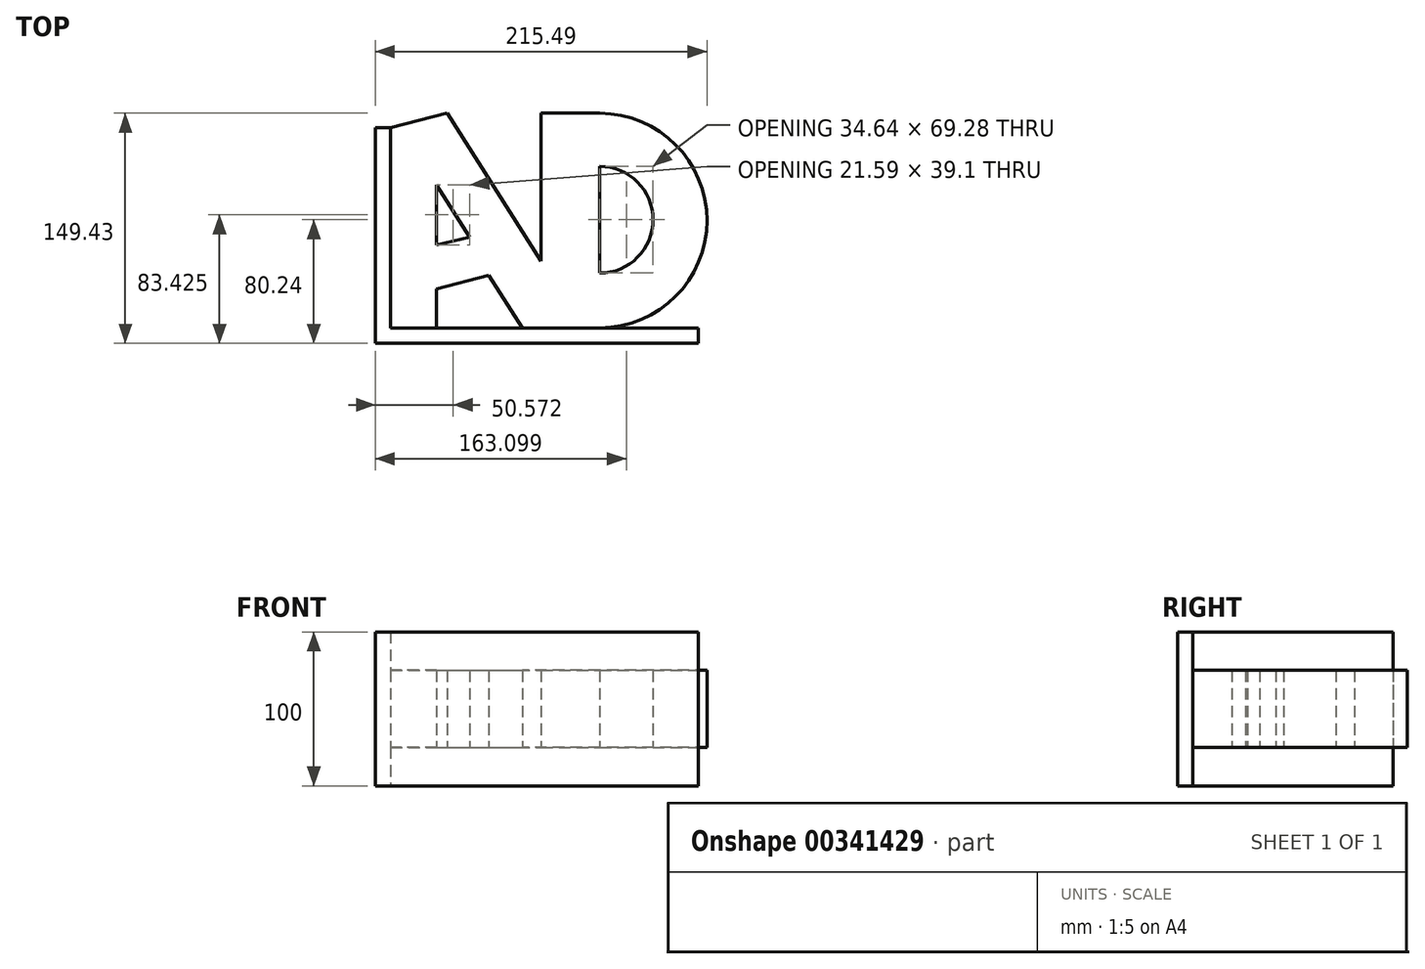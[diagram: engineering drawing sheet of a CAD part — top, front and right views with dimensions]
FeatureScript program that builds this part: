
annotation { "Feature Type Name" : "Feature", "Feature Type Description" : "" }
export const myFeature = defineFeature(function(context is Context, id is Id, definition is map)
    precondition{}
    {
        {
            var Q0;
            Q0=qCreatedBy(makeId("Top.planeOp"),FACE);
            var sketch = newSketch(context, id + "F0", { "sketchPlane" : qUnion([Q0])});
            skLineSegment(sketch, "E0", {"start": v(-97.78, 0) * mm, "end": v(102.22, 0) * mm});
            skLineSegment(sketch, "E1", {"start": v(-97.78, 10) * mm, "end": v(-97.78, 140) * mm});
            skLineSegment(sketch, "E2", {"start": v(-97.78, 140) * mm, "end": v(-60.97, 149.43) * mm});
            skLineSegment(sketch, "E3", {"start": v(-60.97, 149.43) * mm, "end": v(0, 53.26) * mm});
            skLineSegment(sketch, "E4", {"start": v(0, 53.26) * mm, "end": v(0, 149.43) * mm});
            skLineSegment(sketch, "E5", {"start": v(0, 149.43) * mm, "end": v(38, 149.43) * mm});
            skLineSegment(sketch, "E6", {"start": v(102.22, 0) * mm, "end": v(102.22, 10) * mm});
            skLineSegment(sketch, "E7", {"start": v(102.22, 10) * mm, "end": v(38, 10) * mm});
            skArc(sketch, "E8", {"start": v(38, 149.43) * mm, "mid": v(107.71, 79.71) * mm, "end": v(38, 10) * mm});
            skLineSegment(sketch, "E9", {"start": v(38, 114.88) * mm, "end": v(38, 45.6) * mm});
            skArc(sketch, "E10", {"start": v(38, 114.88) * mm, "mid": v(72.64, 80.24) * mm, "end": v(38, 45.6) * mm});
            skPoint(sketch, "E11.end.orphan", {"position": v(0, 114.88) * mm});
            skPoint(sketch, "E12.start.orphan", {"position": v(0, 10) * mm});
            skPoint(sketch, "E13.end.orphan", {"position": v(-8.4, 10) * mm});
            skPoint(sketch, "E14.start.orphan", {"position": v(-68, 10) * mm});
            skPoint(sketch, "E15.end.orphan", {"position": v(-26.25, 10) * mm});
            skPoint(sketch, "E16.end.orphan", {"position": v(-19.02, 10) * mm});
            skPoint(sketch, "E17.start.orphan", {"position": v(-56.9, 10) * mm});
            skPoint(sketch, "E18.orphan", {"position": v(-35.1, 10) * mm});
            skLineSegment(sketch, "E19", {"start": v(-68, 10) * mm, "end": v(-68, 35.4) * mm});
            skLineSegment(sketch, "E20", {"start": v(-68, 35.4) * mm, "end": v(-33.96, 44.12) * mm});
            skLineSegment(sketch, "E21", {"start": v(-33.96, 44.12) * mm, "end": v(-12.33, 10) * mm});
            skLineSegment(sketch, "E22", {"start": v(-12.33, 10) * mm, "end": v(-68, 10) * mm});
            skPoint(sketch, "E23.start.orphan", {"position": v(-68, 63.88) * mm});
            skLineSegment(sketch, "E24", {"start": v(-68, 63.88) * mm, "end": v(-68, 102.98) * mm});
            skLineSegment(sketch, "E25", {"start": v(-68, 102.98) * mm, "end": v(-46.41, 68.92) * mm});
            skLineSegment(sketch, "E26", {"start": v(-68, 63.88) * mm, "end": v(-46.41, 68.92) * mm});
            skLineSegment(sketch, "E27", {"start": v(38, 10) * mm, "end": v(-12.33, 10) * mm});
            skLineSegment(sketch, "E28", {"start": v(-68, 10) * mm, "end": v(-97.78, 10) * mm});
            skLineSegment(sketch, "E29", {"start": v(-97.78, 0) * mm, "end": v(-107.78, 0) * mm});
            skLineSegment(sketch, "E30", {"start": v(-107.78, 0) * mm, "end": v(-107.78, 140) * mm});
            skLineSegment(sketch, "E31", {"start": v(-107.78, 140) * mm, "end": v(-97.78, 140) * mm});
            skSolve(sketch);
        }
        {
            var Q0;
            Q0=makeQuery(id+"F0.imprint","IMPRINT",FACE,{"disambiguationData":[TD([[makeQuery(id+"F0.imprint","IMPRINT",EDGE,{"derivedFrom":sQuery(id+"F0.wireOp",EDGE,"E0")}),1.0]])]});
            extrude(context, id + "F1", {"entities" : qUnion([Q0]), "depth" : 100 * mm});
        }
        {
            var Q0;
            {var subQ0=sQuery(id+"F0.wireOp",EDGE,"E2");Q0=makeQuery(id+"F0.imprint","IMPRINT",FACE,{"disambiguationData":[TD([[makeQuery(id+"F0.imprint","IMPRINT",EDGE,{"derivedFrom":subQ0}),-1.0]])]});}
            extrude(context, id + "F2", {"entities" : qUnion([Q0]), "operationType" : NewBodyOperationType.ADD, "depth" : 75 * mm});
        }
        {
            var Q0;
            {var subQ0=sQuery(id+"F0.wireOp",EDGE,"E2");Q0=makeQuery(id+"F0.imprint","IMPRINT",FACE,{"disambiguationData":[TD([[makeQuery(id+"F0.imprint","IMPRINT",EDGE,{"derivedFrom":subQ0}),-1.0]])]});}
            extrude(context, id + "F3", {"entities" : qUnion([Q0]), "operationType" : NewBodyOperationType.REMOVE, "depth" : 25 * mm});
        }
    });
